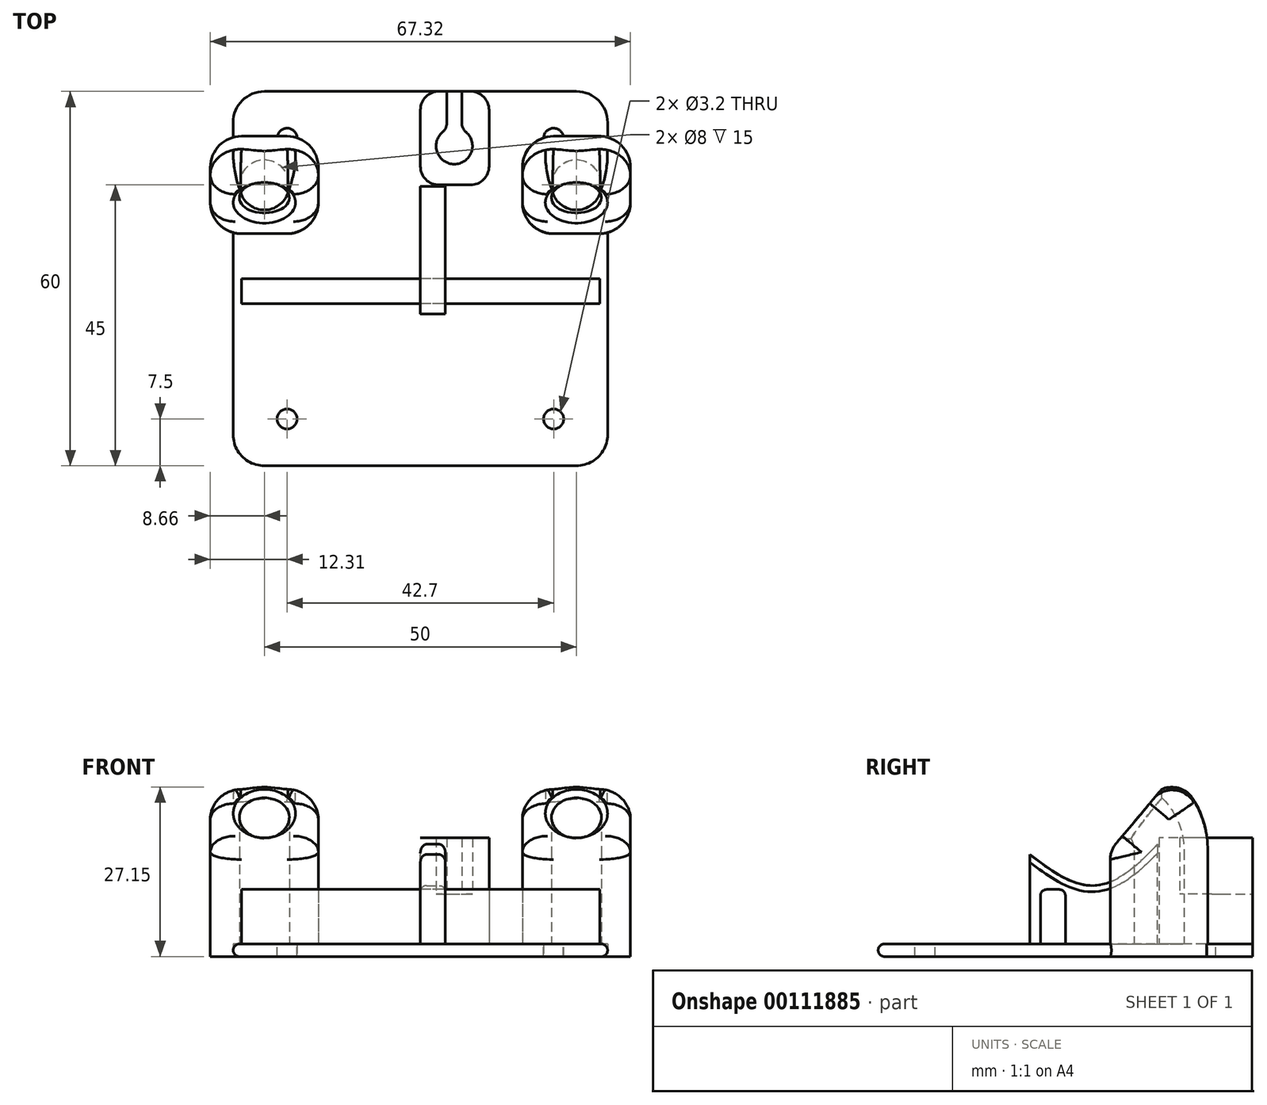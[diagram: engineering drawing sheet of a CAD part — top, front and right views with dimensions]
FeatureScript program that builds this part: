
annotation { "Feature Type Name" : "Feature", "Feature Type Description" : "" }
export const myFeature = defineFeature(function(context is Context, id is Id, definition is map)
    precondition{}
    {
        {
            var Q0;
            Q0=qCreatedBy(makeId("Top.planeOp"),FACE);
            var sketch = newSketch(context, id + "F0", { "sketchPlane" : qUnion([Q0])});
            skArc(sketch, "E0", {"start": v(25, -30) * mm, "mid": v(28.54, -28.54) * mm, "end": v(30, -25) * mm});
            skLineSegment(sketch, "E1", {"start": v(25, -30) * mm, "end": v(-25, -30) * mm});
            skArc(sketch, "E2", {"start": v(30, 25) * mm, "mid": v(28.54, 28.54) * mm, "end": v(25, 30) * mm});
            skLineSegment(sketch, "E3", {"start": v(30, 25) * mm, "end": v(30, -25) * mm});
            skArc(sketch, "E4", {"start": v(-25, 30) * mm, "mid": v(-28.54, 28.54) * mm, "end": v(-30, 25) * mm});
            skLineSegment(sketch, "E5", {"start": v(-25, 30) * mm, "end": v(25, 30) * mm});
            skArc(sketch, "E6", {"start": v(-30, -25) * mm, "mid": v(-28.54, -28.54) * mm, "end": v(-25, -30) * mm});
            skLineSegment(sketch, "E7", {"start": v(-30, -25) * mm, "end": v(-30, 25) * mm});
            skCircle(sketch, "E8", {"center": v(21.35, 22.5) * mm, "radius": 3.25 * mm});
            skCircle(sketch, "E9", {"center": v(21.35, -22.5) * mm, "radius": 3.25 * mm});
            skCircle(sketch, "E10", {"center": v(-21.35, 22.5) * mm, "radius": 3.25 * mm});
            skCircle(sketch, "E11", {"center": v(-21.35, -22.5) * mm, "radius": 3.25 * mm});
            skCircle(sketch, "E12", {"center": v(-21.35, 22.5) * mm, "radius": 4.5 * mm});
            skCircle(sketch, "E13", {"center": v(21.35, 22.5) * mm, "radius": 4.5 * mm});
            skCircle(sketch, "E14", {"center": v(21.35, -22.5) * mm, "radius": 4.5 * mm});
            skCircle(sketch, "E15", {"center": v(-21.35, -22.5) * mm, "radius": 4.5 * mm});
            skCircle(sketch, "E16", {"center": v(-21.35, 22.5) * mm, "radius": 1.6 * mm});
            skCircle(sketch, "E17", {"center": v(21.35, 22.5) * mm, "radius": 1.6 * mm});
            skCircle(sketch, "E18", {"center": v(21.35, -22.5) * mm, "radius": 1.6 * mm});
            skCircle(sketch, "E19", {"center": v(-21.35, -22.5) * mm, "radius": 1.6 * mm});
            skSolve(sketch);
        }
        {
            var Q0;
            Q0=qCreatedBy(makeId("Top.planeOp"),FACE);
            var sketch = newSketch(context, id + "F1", { "sketchPlane" : qUnion([Q0])});
            skLineSegment(sketch, "E20", {"start": v(-48.6, 15) * mm, "end": v(60.7, 15) * mm, "construction": true});
            skLineSegment(sketch, "E21", {"start": v(0, 64.77) * mm, "end": v(0, -51.05) * mm, "construction": true});
            skLineSegment(sketch, "E22", {"start": v(5.5, 55.23) * mm, "end": v(5.5, -47.1) * mm, "construction": true});
            skLineSegment(sketch, "E23", {"start": v(-25, 40.32) * mm, "end": v(-25, -3.03) * mm, "construction": true});
            skLineSegment(sketch, "E24", {"start": v(25, 40.97) * mm, "end": v(25, -7.33) * mm, "construction": true});
            skCircle(sketch, "E25", {"center": v(-25, 15) * mm, "radius": 4 * mm});
            skCircle(sketch, "E26", {"center": v(25, 15) * mm, "radius": 4 * mm});
            skCircle(sketch, "E27", {"center": v(5.5, 21.16) * mm, "radius": 2.9 * mm});
            skCircle(sketch, "E28", {"center": v(5.5, -21.16) * mm, "radius": 3.1 * mm});
            skLineSegment(sketch, "E29.bottom", {"start": v(6.7, 23.81) * mm, "end": v(4.3, 23.81) * mm});
            skLineSegment(sketch, "E29.top", {"start": v(6.7, 30.96) * mm, "end": v(4.3, 30.96) * mm});
            skLineSegment(sketch, "E29.left", {"start": v(6.7, 23.81) * mm, "end": v(6.7, 30.96) * mm});
            skLineSegment(sketch, "E29.right", {"start": v(4.3, 23.81) * mm, "end": v(4.3, 30.96) * mm});
            skPoint(sketch, "E29.middle", {"position": v(5.5, 27.39) * mm});
            skLineSegment(sketch, "E30.bottom", {"start": v(0, 30) * mm, "end": v(11, 30) * mm});
            skLineSegment(sketch, "E30.top", {"start": v(0, 15) * mm, "end": v(11, 15) * mm});
            skLineSegment(sketch, "E30.left", {"start": v(0, 30) * mm, "end": v(0, 15) * mm});
            skLineSegment(sketch, "E30.right", {"start": v(11, 30) * mm, "end": v(11, 15) * mm});
            skLineSegment(sketch, "E31.bottom", {"start": v(-28.66, 22.81) * mm, "end": v(-21.34, 22.81) * mm});
            skLineSegment(sketch, "E31.top", {"start": v(-28.66, 7.19) * mm, "end": v(-21.34, 7.19) * mm});
            skLineSegment(sketch, "E31.left", {"start": v(-33.66, 17.81) * mm, "end": v(-33.66, 12.19) * mm});
            skLineSegment(sketch, "E31.right", {"start": v(-16.34, 17.81) * mm, "end": v(-16.34, 12.19) * mm});
            skLineSegment(sketch, "E32.bottom", {"start": v(21.34, 22.81) * mm, "end": v(28.66, 22.81) * mm});
            skLineSegment(sketch, "E32.top", {"start": v(21.34, 7.19) * mm, "end": v(28.66, 7.19) * mm});
            skLineSegment(sketch, "E32.left", {"start": v(16.34, 17.81) * mm, "end": v(16.34, 12.19) * mm});
            skLineSegment(sketch, "E32.right", {"start": v(33.66, 17.81) * mm, "end": v(33.66, 12.19) * mm});
            skPoint(sketch, "E33.visualSharp", {"position": v(-33.66, 22.81) * mm});
            skArc(sketch, "E33.filletArc", {"start": v(-28.66, 22.81) * mm, "mid": v(-32.2, 21.35) * mm, "end": v(-33.66, 17.81) * mm});
            skPoint(sketch, "E34.visualSharp", {"position": v(-16.34, 22.81) * mm});
            skArc(sketch, "E34.filletArc", {"start": v(-16.34, 17.81) * mm, "mid": v(-17.8, 21.35) * mm, "end": v(-21.34, 22.81) * mm});
            skPoint(sketch, "E35.visualSharp", {"position": v(-16.34, 7.19) * mm});
            skArc(sketch, "E35.filletArc", {"start": v(-21.34, 7.19) * mm, "mid": v(-17.8, 8.65) * mm, "end": v(-16.34, 12.19) * mm});
            skPoint(sketch, "E36.visualSharp", {"position": v(-33.66, 7.19) * mm});
            skArc(sketch, "E36.filletArc", {"start": v(-33.66, 12.19) * mm, "mid": v(-32.2, 8.65) * mm, "end": v(-28.66, 7.19) * mm});
            skPoint(sketch, "E37.visualSharp", {"position": v(16.34, 22.81) * mm});
            skArc(sketch, "E37.filletArc", {"start": v(21.34, 22.81) * mm, "mid": v(17.8, 21.35) * mm, "end": v(16.34, 17.81) * mm});
            skPoint(sketch, "E38.visualSharp", {"position": v(33.66, 22.81) * mm});
            skArc(sketch, "E38.filletArc", {"start": v(33.66, 17.81) * mm, "mid": v(32.2, 21.35) * mm, "end": v(28.66, 22.81) * mm});
            skPoint(sketch, "E39.visualSharp", {"position": v(16.34, 7.19) * mm});
            skArc(sketch, "E39.filletArc", {"start": v(16.34, 12.19) * mm, "mid": v(17.8, 8.65) * mm, "end": v(21.34, 7.19) * mm});
            skPoint(sketch, "E40.visualSharp", {"position": v(33.66, 7.19) * mm});
            skArc(sketch, "E40.filletArc", {"start": v(28.66, 7.19) * mm, "mid": v(32.2, 8.65) * mm, "end": v(33.66, 12.19) * mm});
            skSolve(sketch);
        }
        {
            var Q0;
            Q0=makeQuery(id+"F1.imprint","IMPRINT",FACE,{"disambiguationData":[TD([[makeQuery(id+"F1.imprint","IMPRINT",EDGE,{"derivedFrom":sQuery(id+"F1.wireOp",EDGE,"E30.top")}),1.0]])]});
            var Q1;
            {var subQ0=sQuery(id+"F1.wireOp",EDGE,"E29.bottom");Q1=makeQuery(id+"F1.imprint","IMPRINT",FACE,{"disambiguationData":[TD([[makeQuery(id+"F1.imprint","IMPRINT",EDGE,{"derivedFrom":subQ0}),1.0]])]});}
            var Q2;
            {var subQ0=sQuery(id+"F1.wireOp",EDGE,"E29.left");var subQ6=sQuery(id+"F1.wireOp",EDGE,"E30.bottom");var subQ7=makeQuery(id+"F1.imprint","INTERSECT",VERTEX,{"derivedFrom":[subQ0,subQ6]});Q2=makeQuery(id+"F1.imprint","IMPRINT",FACE,{"disambiguationData":[TD([[makeQuery(id+"F1.imprint","IMPRINT",EDGE,{"disambiguationData":[TD([[subQ7,1.0]])],"derivedFrom":subQ6}),-1.0]])]});}
            var Q3;
            {var subQ0=sQuery(id+"F1.wireOp",EDGE,"E29.bottom");Q3=makeQuery(id+"F1.imprint","IMPRINT",FACE,{"disambiguationData":[TD([[makeQuery(id+"F1.imprint","IMPRINT",EDGE,{"derivedFrom":subQ0}),-1.0]])]});}
            extrude(context, id + "F2", {"entities" : qUnion([Q0, Q1, Q2, Q3]), "depth" : 8 * mm});
        }
        {
            var Q0;
            Q0=makeQuery(id+"F0.imprint","IMPRINT",FACE,{"disambiguationData":[TD([[makeQuery(id+"F0.imprint","IMPRINT",EDGE,{"derivedFrom":sQuery(id+"F0.wireOp",EDGE,"E0")}),1.0]])]});
            var Q1;
            Q1=makeQuery(id+"F0.imprint","IMPRINT",FACE,{"disambiguationData":[TD([[makeQuery(id+"F0.imprint","IMPRINT",EDGE,{"derivedFrom":sQuery(id+"F0.wireOp",EDGE,"E10")}),1.0]])]});
            var Q2;
            Q2=makeQuery(id+"F0.imprint","IMPRINT",FACE,{"disambiguationData":[TD([[makeQuery(id+"F0.imprint","IMPRINT",EDGE,{"derivedFrom":sQuery(id+"F0.wireOp",EDGE,"E10")}),-1.0]])]});
            var Q3;
            Q3=makeQuery(id+"F0.imprint","IMPRINT",FACE,{"disambiguationData":[TD([[makeQuery(id+"F0.imprint","IMPRINT",EDGE,{"derivedFrom":sQuery(id+"F0.wireOp",EDGE,"E8")}),1.0]])]});
            var Q4;
            Q4=makeQuery(id+"F0.imprint","IMPRINT",FACE,{"disambiguationData":[TD([[makeQuery(id+"F0.imprint","IMPRINT",EDGE,{"derivedFrom":sQuery(id+"F0.wireOp",EDGE,"E8")}),-1.0]])]});
            var Q5;
            Q5=makeQuery(id+"F0.imprint","IMPRINT",FACE,{"disambiguationData":[TD([[makeQuery(id+"F0.imprint","IMPRINT",EDGE,{"derivedFrom":sQuery(id+"F0.wireOp",EDGE,"E9")}),1.0]])]});
            var Q6;
            Q6=makeQuery(id+"F0.imprint","IMPRINT",FACE,{"disambiguationData":[TD([[makeQuery(id+"F0.imprint","IMPRINT",EDGE,{"derivedFrom":sQuery(id+"F0.wireOp",EDGE,"E9")}),-1.0]])]});
            var Q7;
            Q7=makeQuery(id+"F0.imprint","IMPRINT",FACE,{"disambiguationData":[TD([[makeQuery(id+"F0.imprint","IMPRINT",EDGE,{"derivedFrom":sQuery(id+"F0.wireOp",EDGE,"E11")}),1.0]])]});
            var Q8;
            Q8=makeQuery(id+"F0.imprint","IMPRINT",FACE,{"disambiguationData":[TD([[makeQuery(id+"F0.imprint","IMPRINT",EDGE,{"derivedFrom":sQuery(id+"F0.wireOp",EDGE,"E11")}),-1.0]])]});
            extrude(context, id + "F3", {"entities" : qUnion([Q0, Q1, Q2, Q3, Q4, Q5, Q6, Q7, Q8]), "oppositeDirection" : true, "depth" : 2 * mm});
        }
        {
            var Q0;
            Q0=makeQuery(id+"F2.opExtrude","CAP_FACE",FACE,{"disambiguationData":[OSD([sQuery(id+"F1.wireOp",EDGE,"E30.bottom"),sQuery(id+"F1.wireOp",EDGE,"E30.top"),sQuery(id+"F1.wireOp",EDGE,"E30.left"),sQuery(id+"F1.wireOp",EDGE,"E30.right")])],"isStart":false});
            var sketch = newSketch(context, id + "F4", { "sketchPlane" : qUnion([Q0])});
            skCircle(sketch, "E41", {"center": v(5.43, 21.25) * mm, "radius": 2.9 * mm});
            skLineSegment(sketch, "E42.bottom", {"start": v(6.63, 23.9) * mm, "end": v(4.23, 23.9) * mm});
            skLineSegment(sketch, "E42.top", {"start": v(6.63, 31.05) * mm, "end": v(4.23, 31.05) * mm});
            skLineSegment(sketch, "E42.left", {"start": v(6.63, 23.9) * mm, "end": v(6.63, 31.05) * mm});
            skLineSegment(sketch, "E42.right", {"start": v(4.23, 23.9) * mm, "end": v(4.23, 31.05) * mm});
            skPoint(sketch, "E42.middle", {"position": v(5.43, 27.47) * mm});
            skLineSegment(sketch, "E43.bottom", {"start": v(0, 30) * mm, "end": v(11, 30) * mm});
            skLineSegment(sketch, "E43.top", {"start": v(0, 15) * mm, "end": v(11, 15) * mm});
            skLineSegment(sketch, "E43.left", {"start": v(0, 30) * mm, "end": v(0, 15) * mm});
            skLineSegment(sketch, "E43.right", {"start": v(11, 30) * mm, "end": v(11, 15) * mm});
            skSolve(sketch);
        }
        {
            var Q0;
            {var subQ0=sQuery(id+"F4.wireOp",EDGE,"E43.right");var subQ1=sQuery(id+"F4.wireOp",EDGE,"E43.top");var subQ2=makeQuery(id+"F4.imprint","INTERSECT",VERTEX,{"derivedFrom":[subQ1,subQ0]});Q0=makeQuery(id+"F4.imprint","IMPRINT",FACE,{"disambiguationData":[TD([[makeQuery(id+"F4.imprint","IMPRINT",EDGE,{"disambiguationData":[TD([[subQ2,1.0]])],"derivedFrom":subQ1}),1.0]])]});}
            extrude(context, id + "F5", {"entities" : qUnion([Q0]), "operationType" : NewBodyOperationType.ADD, "depth" : 9 * mm});
        }
        {
            var Q0;
            Q0=makeQuery(id+"F5.opExtrude","SWEPT_EDGE",EDGE,{"disambiguationData":[OSD([sQuery(id+"F4.wireOp",EDGE,"E41"),sQuery(id+"F4.wireOp",EDGE,"E42.bottom"),sQuery(id+"F4.wireOp",EDGE,"E42.left")])]});
            var Q1;
            Q1=makeQuery(id+"F5.opExtrude","SWEPT_EDGE",EDGE,{"disambiguationData":[OSD([sQuery(id+"F4.wireOp",EDGE,"E41"),sQuery(id+"F4.wireOp",EDGE,"E42.bottom"),sQuery(id+"F4.wireOp",EDGE,"E42.right")])]});
            fillet(context, id + "F6", {"entities" : qUnion([Q0, Q1]), "radius" : 2 * mm, "tangentPropagation" : true, "allowEdgeOverflow" : false});
        }
        {
            var Q0;
            Q0=qCreatedBy(makeId("Right.planeOp"),FACE);
            var sketch = newSketch(context, id + "F7", { "sketchPlane" : qUnion([Q0])});
            skFitSpline(sketch, "E44", {"points": [v(14.76, 16) * mm, v(-5.68, 14.35) * mm], "startDerivative": vector(-24.35, -26.04) * mm, "endDerivative": vector(-25.64, 20.3) * mm});
            skLineSegment(sketch, "E45", {"start": v(-5.68, 14.35) * mm, "end": v(-5.68, 0) * mm});
            skLineSegment(sketch, "E46", {"start": v(-5.68, 0) * mm, "end": v(14.76, 0) * mm});
            skLineSegment(sketch, "E47", {"start": v(14.76, 0) * mm, "end": v(14.76, 16) * mm});
            skSolve(sketch);
        }
        {
            var Q0;
            Q0=qSketchRegion(id+"F7",true);
            extrude(context, id + "F8", {"entities" : qUnion([Q0]), "depth" : 4 * mm});
        }
        {
            var Q0;
            Q0=makeQuery(id+"F5.boolean.opBoolean","MERGE",EDGE,{"derivedFrom":[makeQuery(id+"F2.opExtrude","SWEPT_EDGE",EDGE,{"disambiguationData":[OSD([sQuery(id+"F1.wireOp",EDGE,"E30.top"),sQuery(id+"F1.wireOp",EDGE,"E30.right")])]}),makeQuery(id+"F5.opExtrude","SWEPT_EDGE",EDGE,{"disambiguationData":[OSD([sQuery(id+"F4.wireOp",EDGE,"E43.top"),sQuery(id+"F4.wireOp",EDGE,"E43.right")])]})]});
            var Q1;
            Q1=makeQuery(id+"F5.boolean.opBoolean","MERGE",EDGE,{"derivedFrom":[makeQuery(id+"F2.opExtrude","SWEPT_EDGE",EDGE,{"disambiguationData":[OSD([sQuery(id+"F1.wireOp",EDGE,"E30.bottom"),sQuery(id+"F1.wireOp",EDGE,"E30.right")])]}),makeQuery(id+"F5.opExtrude","SWEPT_EDGE",EDGE,{"disambiguationData":[OSD([sQuery(id+"F4.wireOp",EDGE,"E43.bottom"),sQuery(id+"F4.wireOp",EDGE,"E43.right")])]})]});
            var Q2;
            Q2=makeQuery(id+"F5.boolean.opBoolean","MERGE",EDGE,{"derivedFrom":[makeQuery(id+"F2.opExtrude","SWEPT_EDGE",EDGE,{"disambiguationData":[OSD([sQuery(id+"F1.wireOp",EDGE,"E30.bottom"),sQuery(id+"F1.wireOp",EDGE,"E30.left")])]}),makeQuery(id+"F5.opExtrude","SWEPT_EDGE",EDGE,{"disambiguationData":[OSD([sQuery(id+"F4.wireOp",EDGE,"E43.bottom"),sQuery(id+"F4.wireOp",EDGE,"E43.left")])]})]});
            var Q3;
            Q3=makeQuery(id+"F5.boolean.opBoolean","MERGE",EDGE,{"derivedFrom":[makeQuery(id+"F2.opExtrude","SWEPT_EDGE",EDGE,{"disambiguationData":[OSD([sQuery(id+"F1.wireOp",EDGE,"E30.top"),sQuery(id+"F1.wireOp",EDGE,"E30.left")])]}),makeQuery(id+"F5.opExtrude","SWEPT_EDGE",EDGE,{"disambiguationData":[OSD([sQuery(id+"F4.wireOp",EDGE,"E43.top"),sQuery(id+"F4.wireOp",EDGE,"E43.left")])]})]});
            fillet(context, id + "F9", {"entities" : qUnion([Q0, Q1, Q2, Q3]), "radius" : 3 * mm, "tangentPropagation" : true, "allowEdgeOverflow" : false});
        }
        {
            var Q0;
            Q0=makeQuery(id+"F1.imprint","IMPRINT",FACE,{"disambiguationData":[TD([[makeQuery(id+"F1.imprint","IMPRINT",EDGE,{"derivedFrom":sQuery(id+"F1.wireOp",EDGE,"E25")}),-1.0]])]});
            var Q1;
            Q1=makeQuery(id+"F1.imprint","IMPRINT",FACE,{"disambiguationData":[TD([[makeQuery(id+"F1.imprint","IMPRINT",EDGE,{"derivedFrom":sQuery(id+"F1.wireOp",EDGE,"E26")}),-1.0]])]});
            extrude(context, id + "F10", {"entities" : qUnion([Q0, Q1]), "depth" : 15 * mm});
        }
        {
            var Q0;
            Q0=makeQuery(id+"F10.opExtrude","CAP_FACE",FACE,{"disambiguationData":[OSD([sQuery(id+"F1.wireOp",EDGE,"E25"),sQuery(id+"F1.wireOp",EDGE,"E31.bottom"),sQuery(id+"F1.wireOp",EDGE,"E31.top"),sQuery(id+"F1.wireOp",EDGE,"E31.left"),sQuery(id+"F1.wireOp",EDGE,"E31.right"),sQuery(id+"F1.wireOp",EDGE,"E33.filletArc"),sQuery(id+"F1.wireOp",EDGE,"E34.filletArc"),sQuery(id+"F1.wireOp",EDGE,"E35.filletArc"),sQuery(id+"F1.wireOp",EDGE,"E36.filletArc")])],"isStart":false});
            var Q1;
            Q1=makeQuery(id+"F10.opExtrude","CAP_FACE",FACE,{"disambiguationData":[OSD([sQuery(id+"F1.wireOp",EDGE,"E26"),sQuery(id+"F1.wireOp",EDGE,"E32.bottom"),sQuery(id+"F1.wireOp",EDGE,"E32.top"),sQuery(id+"F1.wireOp",EDGE,"E32.left"),sQuery(id+"F1.wireOp",EDGE,"E32.right"),sQuery(id+"F1.wireOp",EDGE,"E37.filletArc"),sQuery(id+"F1.wireOp",EDGE,"E38.filletArc"),sQuery(id+"F1.wireOp",EDGE,"E39.filletArc"),sQuery(id+"F1.wireOp",EDGE,"E40.filletArc")])],"isStart":false});
            var Q2;
            Q2=makeQuery(id+"F10.opExtrude","CAP_EDGE",EDGE,{"disambiguationData":[OSD([sQuery(id+"F1.wireOp",EDGE,"E31.top")])],"isStart":false});
            revolve(context, id + "F11", {"operationType" : NewBodyOperationType.ADD, "entities" : qUnion([Q0, Q1]), "axis" : qUnion([Q2]), "revolveType" : RevolveType.ONE_DIRECTION, "angle" : 50 * degree});
        }
        {
            var Q0;
            Q0=makeQuery(id+"F11.opRevolve","CAP_EDGE",EDGE,{"disambiguationData":[OSD([sQuery(id+"F1.wireOp",EDGE,"E25")])],"isStart":false});
            var Q1;
            Q1=makeQuery(id+"F11.opRevolve","CAP_EDGE",EDGE,{"disambiguationData":[OSD([sQuery(id+"F1.wireOp",EDGE,"E26")])],"isStart":false});
            chamfer(context, id + "F12", {"entities" : qUnion([Q0, Q1]), "width" : 1 * mm, "tangentPropagation" : true});
        }
        {
            var Q0;
            Q0=makeQuery(id+"F11.opRevolve","CAP_EDGE",EDGE,{"disambiguationData":[OSD([sQuery(id+"F1.wireOp",EDGE,"E31.bottom")])],"isStart":false});
            var Q1;
            Q1=makeQuery(id+"F11.opRevolve","CAP_EDGE",EDGE,{"disambiguationData":[OSD([sQuery(id+"F1.wireOp",EDGE,"E32.bottom")])],"isStart":false});
            fillet(context, id + "F13", {"entities" : qUnion([Q0, Q1]), "radius" : 4 * mm, "tangentPropagation" : true, "allowEdgeOverflow" : false});
        }
        {
            var Q0;
            Q0=qCreatedBy(makeId("Front.planeOp"),FACE);
            var sketch = newSketch(context, id + "F14", { "sketchPlane" : qUnion([Q0])});
            skLineSegment(sketch, "E48.bottom", {"start": v(28.74, 0) * mm, "end": v(-28.68, 0) * mm});
            skLineSegment(sketch, "E48.top", {"start": v(28.74, 8.74) * mm, "end": v(-28.68, 8.74) * mm});
            skLineSegment(sketch, "E48.left", {"start": v(28.74, 0) * mm, "end": v(28.74, 8.74) * mm});
            skLineSegment(sketch, "E48.right", {"start": v(-28.68, 0) * mm, "end": v(-28.68, 8.74) * mm});
            skSolve(sketch);
        }
        {
            var Q0;
            Q0=qSketchRegion(id+"F14",true);
            extrude(context, id + "F15", {"entities" : qUnion([Q0]), "depth" : 4 * mm});
        }
        {
            var Q0;
            Q0=makeQuery(id+"F10.opExtrude","CAP_FACE",FACE,{"disambiguationData":[OSD([sQuery(id+"F1.wireOp",EDGE,"E26"),sQuery(id+"F1.wireOp",EDGE,"E32.bottom"),sQuery(id+"F1.wireOp",EDGE,"E32.top"),sQuery(id+"F1.wireOp",EDGE,"E32.left"),sQuery(id+"F1.wireOp",EDGE,"E32.right"),sQuery(id+"F1.wireOp",EDGE,"E37.filletArc"),sQuery(id+"F1.wireOp",EDGE,"E38.filletArc"),sQuery(id+"F1.wireOp",EDGE,"E39.filletArc"),sQuery(id+"F1.wireOp",EDGE,"E40.filletArc")])],"isStart":true});
            var Q1;
            Q1=makeQuery(id+"F10.opExtrude","CAP_FACE",FACE,{"disambiguationData":[OSD([sQuery(id+"F1.wireOp",EDGE,"E25"),sQuery(id+"F1.wireOp",EDGE,"E31.bottom"),sQuery(id+"F1.wireOp",EDGE,"E31.top"),sQuery(id+"F1.wireOp",EDGE,"E31.left"),sQuery(id+"F1.wireOp",EDGE,"E31.right"),sQuery(id+"F1.wireOp",EDGE,"E33.filletArc"),sQuery(id+"F1.wireOp",EDGE,"E34.filletArc"),sQuery(id+"F1.wireOp",EDGE,"E35.filletArc"),sQuery(id+"F1.wireOp",EDGE,"E36.filletArc")])],"isStart":true});
            extrude(context, id + "F16", {"entities" : qUnion([Q0, Q1]), "operationType" : NewBodyOperationType.ADD, "depth" : 2 * mm});
        }
        {
            var Q0;
            Q0=makeQuery(id+"F15.opExtrude","CAP_EDGE",EDGE,{"disambiguationData":[OSD([sQuery(id+"F14.wireOp",EDGE,"E48.top")])],"isStart":true});
            var Q1;
            Q1=makeQuery(id+"F15.opExtrude","CAP_EDGE",EDGE,{"disambiguationData":[OSD([sQuery(id+"F14.wireOp",EDGE,"E48.top")])],"isStart":false});
            var Q2;
            Q2=makeQuery(id+"F8.opExtrude","CAP_EDGE",EDGE,{"disambiguationData":[OSD([sQuery(id+"F7.wireOp",EDGE,"E44")])],"isStart":true});
            var Q3;
            Q3=makeQuery(id+"F8.opExtrude","CAP_EDGE",EDGE,{"disambiguationData":[OSD([sQuery(id+"F7.wireOp",EDGE,"E44")])],"isStart":false});
            fillet(context, id + "F17", {"entities" : qUnion([Q0, Q1, Q2, Q3]), "radius" : 1 * mm, "tangentPropagation" : true, "allowEdgeOverflow" : false});
        }
        {
            var Q0;
            Q0=makeQuery(id+"F3.opExtrude","CAP_EDGE",EDGE,{"disambiguationData":[OSD([sQuery(id+"F0.wireOp",EDGE,"E1")])],"isStart":true});
            var Q1;
            Q1=makeQuery(id+"F3.opExtrude","CAP_EDGE",EDGE,{"disambiguationData":[OSD([sQuery(id+"F0.wireOp",EDGE,"E1")])],"isStart":false});
            fillet(context, id + "F18", {"entities" : qUnion([Q0, Q1]), "radius" : 1 * mm, "tangentPropagation" : true, "allowEdgeOverflow" : false});
        }
    });
